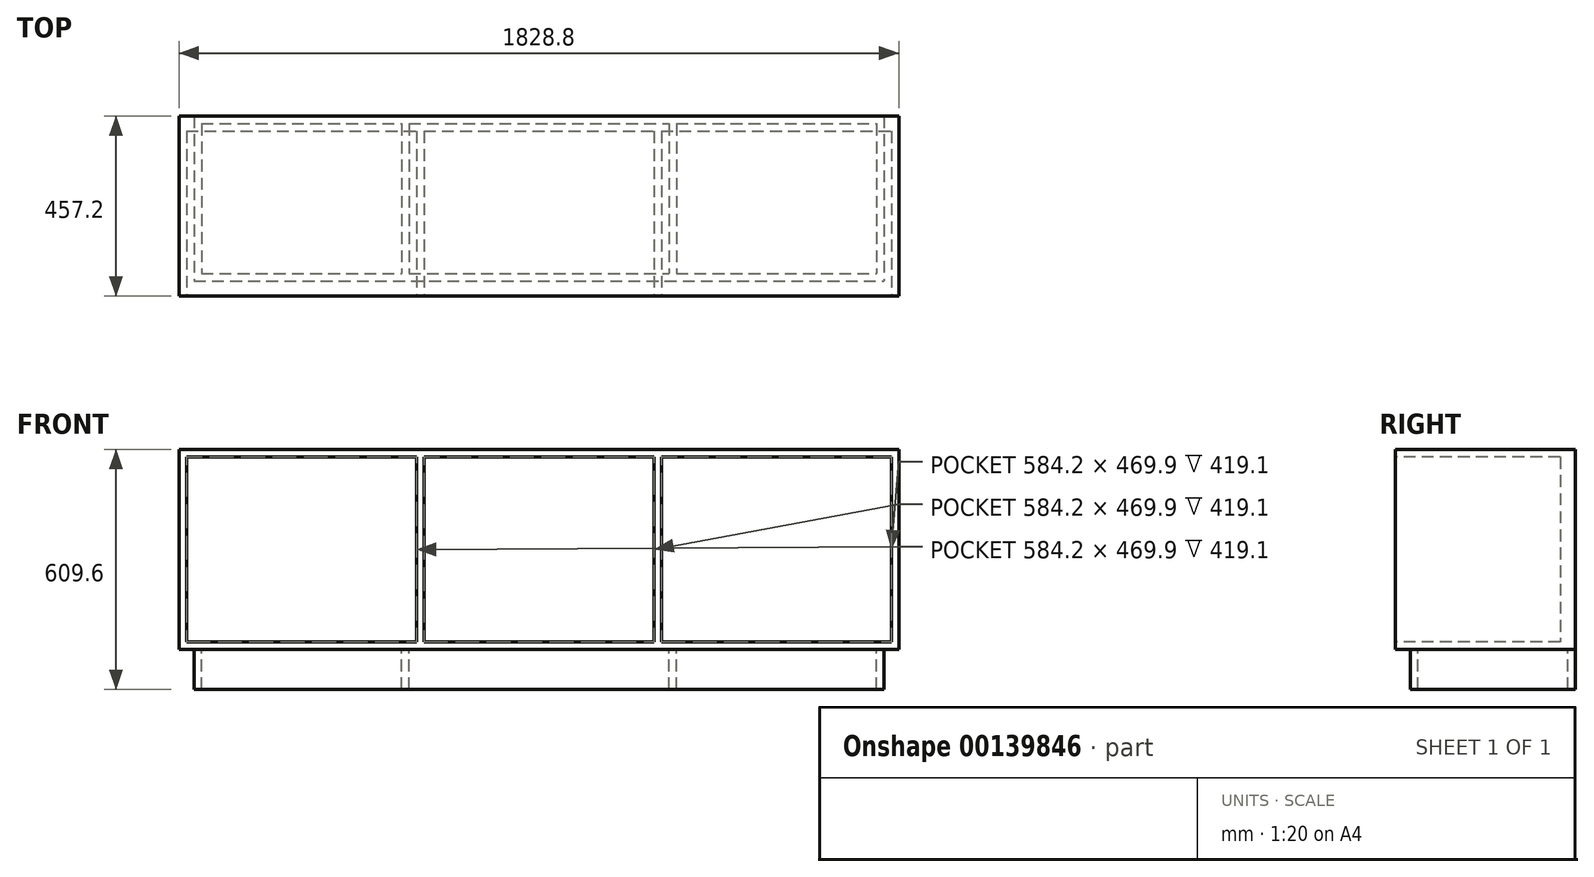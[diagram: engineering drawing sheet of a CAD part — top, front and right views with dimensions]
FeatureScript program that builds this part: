
annotation { "Feature Type Name" : "Feature", "Feature Type Description" : "" }
export const myFeature = defineFeature(function(context is Context, id is Id, definition is map)
    precondition{}
    {
        {
            var Q0;
            Q0=qCreatedBy(makeId("Front.planeOp"),FACE);
            var sketch = newSketch(context, id + "F0", { "sketchPlane" : qUnion([Q0])});
            skLineSegment(sketch, "E0.bottom", {"start": v(0, 0) * mm, "end": v(1828.8, 0) * mm});
            skLineSegment(sketch, "E0.top", {"start": v(0, 508) * mm, "end": v(1828.8, 508) * mm});
            skLineSegment(sketch, "E0.left", {"start": v(0, 0) * mm, "end": v(0, 508) * mm});
            skLineSegment(sketch, "E0.right", {"start": v(1828.8, 0) * mm, "end": v(1828.8, 508) * mm});
            skSolve(sketch);
        }
        {
            var Q0;
            Q0 = qSketchRegion(id + "F0", true);
            extrude(context, id + "F1", {"entities" : qUnion([Q0]), "depth" : 457.2 * mm});
        }
        {
            var Q0;
            Q0=makeQuery(id+"F1.opExtrude","CAP_FACE",FACE,{"disambiguationData":[OSD([sQuery(id+"F0.wireOp",EDGE,"E0.bottom"),sQuery(id+"F0.wireOp",EDGE,"E0.top"),sQuery(id+"F0.wireOp",EDGE,"E0.left"),sQuery(id+"F0.wireOp",EDGE,"E0.right")])],"isStart":false});
            var sketch = newSketch(context, id + "F2", { "sketchPlane" : qUnion([Q0])});
            skLineSegment(sketch, "E1.bottom", {"start": v(19.05, 19.05) * mm, "end": v(603.25, 19.05) * mm});
            skLineSegment(sketch, "E1.top", {"start": v(19.05, 488.95) * mm, "end": v(603.25, 488.95) * mm});
            skLineSegment(sketch, "E1.left", {"start": v(19.05, 19.05) * mm, "end": v(19.05, 488.95) * mm});
            skLineSegment(sketch, "E1.right", {"start": v(603.25, 19.05) * mm, "end": v(603.25, 488.95) * mm});
            skLineSegment(sketch, "E2.bottom", {"start": v(622.3, 488.95) * mm, "end": v(1206.5, 488.95) * mm});
            skLineSegment(sketch, "E2.top", {"start": v(622.3, 19.05) * mm, "end": v(1206.5, 19.05) * mm});
            skLineSegment(sketch, "E2.left", {"start": v(622.3, 488.95) * mm, "end": v(622.3, 19.05) * mm});
            skLineSegment(sketch, "E2.right", {"start": v(1206.5, 488.95) * mm, "end": v(1206.5, 19.05) * mm});
            skLineSegment(sketch, "E3.bottom", {"start": v(1225.55, 488.95) * mm, "end": v(1809.75, 488.95) * mm});
            skLineSegment(sketch, "E3.top", {"start": v(1225.55, 19.05) * mm, "end": v(1809.75, 19.05) * mm});
            skLineSegment(sketch, "E3.left", {"start": v(1225.55, 488.95) * mm, "end": v(1225.55, 19.05) * mm});
            skLineSegment(sketch, "E3.right", {"start": v(1809.75, 488.95) * mm, "end": v(1809.75, 19.05) * mm});
            skSolve(sketch);
        }
        {
            var Q0;
            Q0 = qSketchRegion(id + "F2", true);
            extrude(context, id + "F3", {"entities" : qUnion([Q0]), "operationType" : NewBodyOperationType.REMOVE, "oppositeDirection" : true, "depth" : 419.1 * mm});
        }
        {
            var Q0;
            Q0=makeQuery(id+"F1.opExtrude","SWEPT_FACE",FACE,{"disambiguationData":[OSD([sQuery(id+"F0.wireOp",EDGE,"E0.bottom")])]});
            var sketch = newSketch(context, id + "F4", { "sketchPlane" : qUnion([Q0])});
            skLineSegment(sketch, "E4.bottom", {"start": v(38.1, 0) * mm, "end": v(1790.7, 0) * mm});
            skLineSegment(sketch, "E4.top", {"start": v(38.1, 419.1) * mm, "end": v(1790.7, 419.1) * mm});
            skLineSegment(sketch, "E4.left", {"start": v(38.1, 0) * mm, "end": v(38.1, 419.1) * mm});
            skLineSegment(sketch, "E4.right", {"start": v(1790.7, 0) * mm, "end": v(1790.7, 419.1) * mm});
            skLineSegment(sketch, "E5.0", {"start": v(57.15, 19.05) * mm, "end": v(57.15, 400.05) * mm});
            skLineSegment(sketch, "E5.1", {"start": v(57.15, 19.05) * mm, "end": v(565.15, 19.05) * mm});
            skLineSegment(sketch, "E5.2", {"start": v(1771.65, 19.05) * mm, "end": v(1771.65, 400.05) * mm});
            skLineSegment(sketch, "E5.3", {"start": v(57.15, 400.05) * mm, "end": v(565.15, 400.05) * mm});
            skLineSegment(sketch, "E6.0", {"start": v(-6.35, -6.35) * mm, "end": v(1835.15, -6.35) * mm});
            skLineSegment(sketch, "E6.1", {"start": v(-6.35, 463.55) * mm, "end": v(-6.35, -6.35) * mm});
            skLineSegment(sketch, "E6.2", {"start": v(1835.15, 463.55) * mm, "end": v(-6.35, 463.55) * mm});
            skLineSegment(sketch, "E6.3", {"start": v(1835.15, -6.35) * mm, "end": v(1835.15, 463.55) * mm});
            skLineSegment(sketch, "E7.0", {"start": v(565.15, 19.05) * mm, "end": v(565.15, 400.05) * mm});
            skLineSegment(sketch, "E8.0", {"start": v(584.2, 19.05) * mm, "end": v(584.2, 400.05) * mm});
            skLineSegment(sketch, "E9.0", {"start": v(1263.65, 19.05) * mm, "end": v(1263.65, 400.05) * mm});
            skLineSegment(sketch, "E10.0", {"start": v(1244.6, 19.05) * mm, "end": v(1244.6, 400.05) * mm});
            skLineSegment(sketch, "E11.trimOffspring", {"start": v(1263.65, 400.05) * mm, "end": v(1771.65, 400.05) * mm});
            skLineSegment(sketch, "E12.trimOffspring", {"start": v(1263.65, 19.05) * mm, "end": v(1771.65, 19.05) * mm});
            skLineSegment(sketch, "E13.trimOffspring", {"start": v(584.2, 19.05) * mm, "end": v(1244.6, 19.05) * mm});
            skLineSegment(sketch, "E14.trimOffspring", {"start": v(584.2, 400.05) * mm, "end": v(1244.6, 400.05) * mm});
            skSolve(sketch);
        }
        {
            var Q0;
            Q0=makeQuery(id+"F4.imprint","IMPRINT",FACE,{"disambiguationData":[TD([[makeQuery(id+"F4.imprint","IMPRINT",EDGE,{"derivedFrom":sQuery(id+"F4.wireOp",EDGE,"E4.bottom")}),1.0]])]});
            extrude(context, id + "F5", {"entities" : qUnion([Q0]), "operationType" : NewBodyOperationType.ADD, "depth" : 101.6 * mm});
        }
    });
